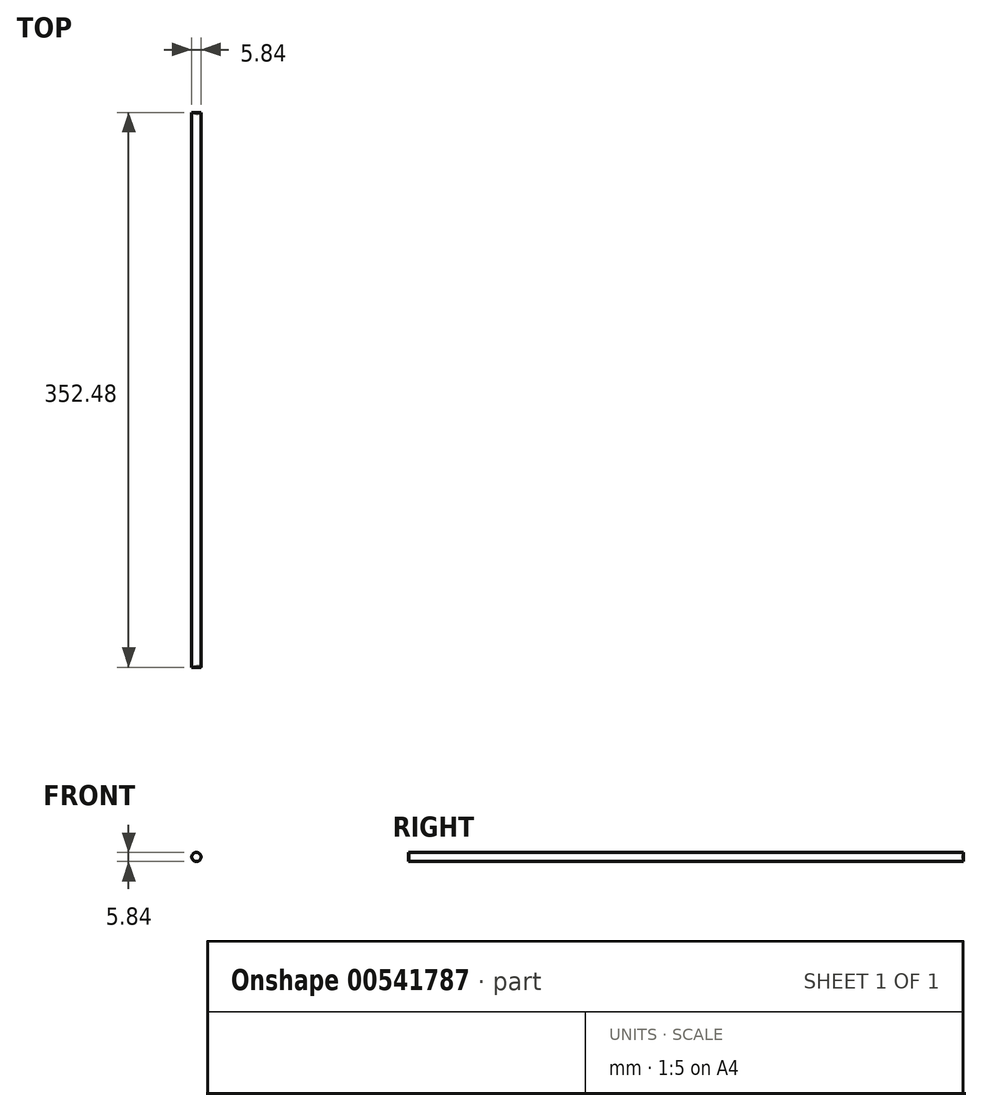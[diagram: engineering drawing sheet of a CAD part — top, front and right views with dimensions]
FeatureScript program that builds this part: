
annotation { "Feature Type Name" : "Feature", "Feature Type Description" : "" }
export const myFeature = defineFeature(function(context is Context, id is Id, definition is map)
    precondition{}
    {
        {
            var Q0;
            Q0=qCreatedBy(makeId("Top.planeOp"),FACE);
            var sketch = newSketch(context, id + "F0", { "sketchPlane" : qUnion([Q0])});
            skLineSegment(sketch, "E0.right", {"start": v(-2.92, 180) * mm, "end": v(-2.92, -180) * mm});
            skPoint(sketch, "E0.middle", {"position": v(0, 0) * mm});
            skCircle(sketch, "E1", {"center": v(0, 180) * mm, "radius": 4.76 * mm});
            skCircle(sketch, "E2", {"center": v(0, -180) * mm, "radius": 4.76 * mm});
            skLineSegment(sketch, "E3", {"start": v(0, 180) * mm, "end": v(0, -180) * mm});
            skLineSegment(sketch, "E4", {"start": v(0, 180) * mm, "end": v(-2.92, 180) * mm});
            skLineSegment(sketch, "E5", {"start": v(0, -180) * mm, "end": v(-2.92, -180) * mm});
            skSolve(sketch);
        }
        {
            var Q0;
            {var subQ0=sQuery(id+"F0.wireOp",EDGE,"E1");var subQ1=sQuery(id+"F0.wireOp",EDGE,"E0.right");var subQ2=makeQuery(id+"F0.imprint","INTERSECT",VERTEX,{"derivedFrom":[subQ1,subQ0]});Q0=makeQuery(id+"F0.imprint","IMPRINT",FACE,{"disambiguationData":[TD([[makeQuery(id+"F0.imprint","IMPRINT",EDGE,{"disambiguationData":[TD([[subQ2,-1.0]])],"derivedFrom":subQ1}),1.0]])]});}
            var Q1;
            Q1=sQuery(id+"F0.wireOp",EDGE,"E3");
            revolve(context, id + "F1", {"entities" : qUnion([Q0]), "axis" : qUnion([Q1]), "revolveType" : RevolveType.FULL});
        }
    });
